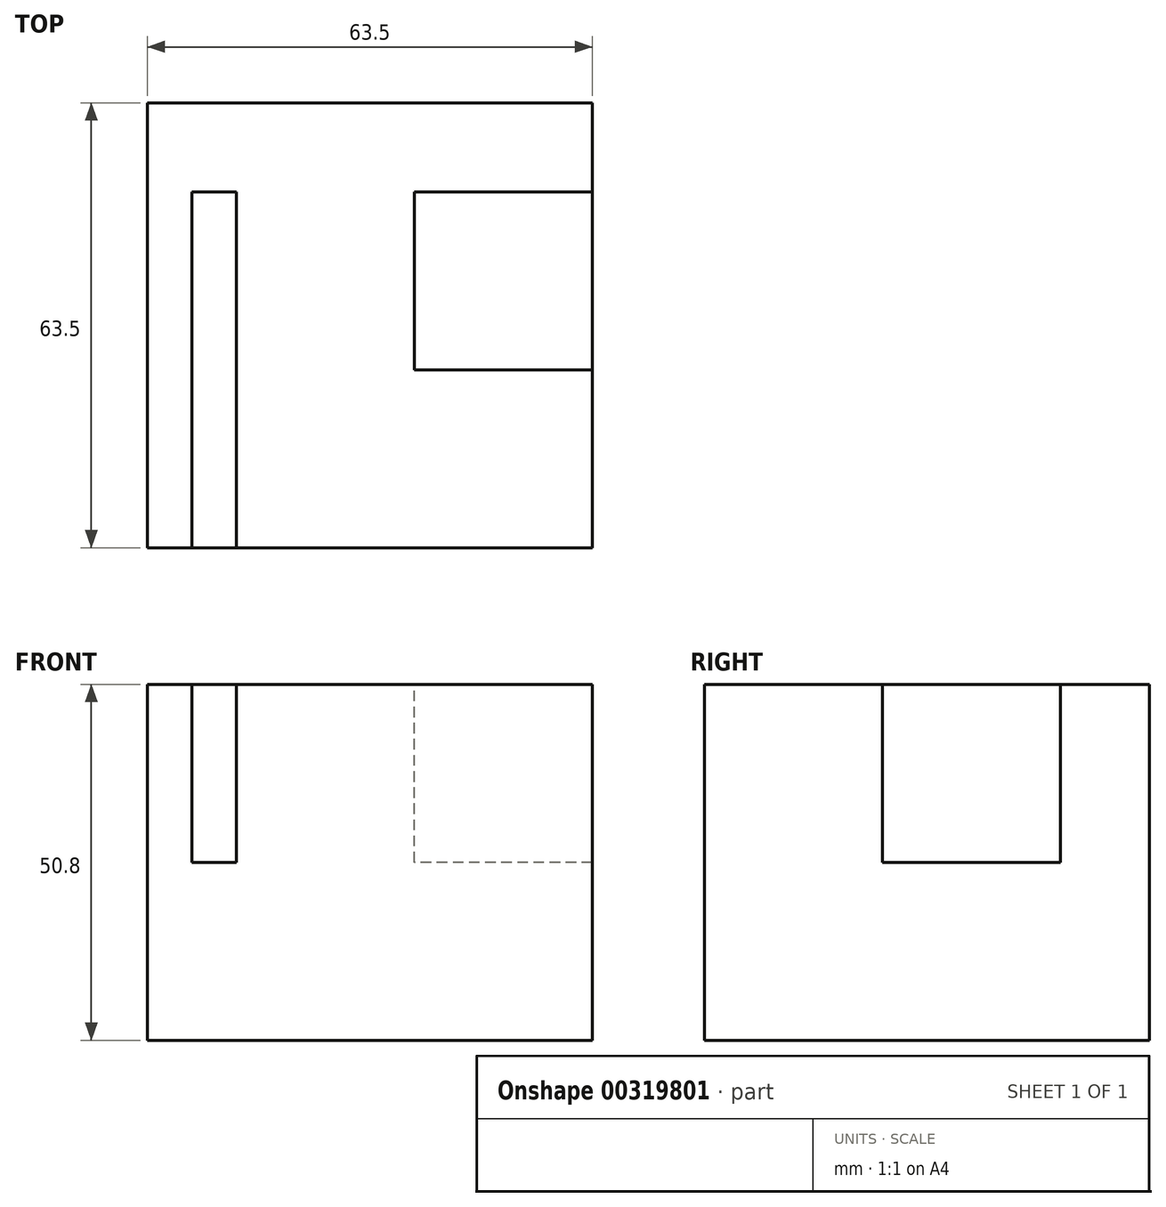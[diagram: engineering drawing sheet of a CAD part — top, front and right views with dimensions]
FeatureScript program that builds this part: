
annotation { "Feature Type Name" : "Feature", "Feature Type Description" : "" }
export const myFeature = defineFeature(function(context is Context, id is Id, definition is map)
    precondition{}
    {
        {
            var Q0;
            Q0=qCreatedBy(makeId("Top.planeOp"),FACE);
            var sketch = newSketch(context, id + "F0", { "sketchPlane" : qUnion([Q0])});
            skLineSegment(sketch, "E0", {"start": v(-27.31, 38.38) * mm, "end": v(36.19, 38.38) * mm});
            skLineSegment(sketch, "E1", {"start": v(36.19, 38.38) * mm, "end": v(36.19, -25.12) * mm});
            skLineSegment(sketch, "E2", {"start": v(36.19, -25.12) * mm, "end": v(-27.31, -25.12) * mm});
            skLineSegment(sketch, "E3", {"start": v(-27.31, -25.12) * mm, "end": v(-27.31, 38.38) * mm});
            skSolve(sketch);
        }
        {
            var Q0;
            Q0=makeQuery(id+"F0.imprint","IMPRINT",FACE,{"disambiguationData":[TD([[makeQuery(id+"F0.imprint","IMPRINT",EDGE,{"derivedFrom":sQuery(id+"F0.wireOp",EDGE,"E0")}),-1.0]])]});
            extrude(context, id + "F1", {"entities" : qUnion([Q0]), "depth" : 50.8 * mm});
        }
        {
            var Q0;
            Q0=makeQuery(id+"F1.opExtrude","CAP_FACE",FACE,{"disambiguationData":[OSD([sQuery(id+"F0.wireOp",EDGE,"E0"),sQuery(id+"F0.wireOp",EDGE,"E1"),sQuery(id+"F0.wireOp",EDGE,"E2"),sQuery(id+"F0.wireOp",EDGE,"E3")])],"isStart":false});
            var sketch = newSketch(context, id + "F2", { "sketchPlane" : qUnion([Q0])});
            skLineSegment(sketch, "E4", {"start": v(-20.96, -25.12) * mm, "end": v(-20.96, 25.68) * mm});
            skLineSegment(sketch, "E5", {"start": v(-20.96, 25.68) * mm, "end": v(-14.61, 25.68) * mm});
            skLineSegment(sketch, "E6", {"start": v(-14.61, 25.68) * mm, "end": v(-14.61, -25.12) * mm});
            skSolve(sketch);
        }
        {
            var Q0;
            {var subQ0=sQuery(id+"F2.wireOp",EDGE,"E4");Q0=makeQuery(id+"F2.imprint","IMPRINT",FACE,{"disambiguationData":[TD([[makeQuery(id+"F2.imprint","IMPRINT",EDGE,{"derivedFrom":subQ0}),-1.0]])]});}
            extrude(context, id + "F3", {"entities" : qUnion([Q0]), "operationType" : NewBodyOperationType.REMOVE, "oppositeDirection" : true, "depth" : 25.4 * mm});
        }
        {
            var Q0;
            Q0=makeQuery(id+"F1.opExtrude","CAP_FACE",FACE,{"disambiguationData":[OSD([sQuery(id+"F0.wireOp",EDGE,"E0"),sQuery(id+"F0.wireOp",EDGE,"E1"),sQuery(id+"F0.wireOp",EDGE,"E2"),sQuery(id+"F0.wireOp",EDGE,"E3")])],"isStart":false});
            var sketch = newSketch(context, id + "F4", { "sketchPlane" : qUnion([Q0])});
            skLineSegment(sketch, "E7", {"start": v(36.19, 0.28) * mm, "end": v(10.79, 0.28) * mm});
            skLineSegment(sketch, "E8", {"start": v(10.79, 0.28) * mm, "end": v(10.79, 25.68) * mm});
            skLineSegment(sketch, "E9", {"start": v(10.79, 25.68) * mm, "end": v(36.19, 25.68) * mm});
            skSolve(sketch);
        }
        {
            var Q0;
            {var subQ0=sQuery(id+"F4.wireOp",EDGE,"E7");Q0=makeQuery(id+"F4.imprint","IMPRINT",FACE,{"disambiguationData":[TD([[makeQuery(id+"F4.imprint","IMPRINT",EDGE,{"derivedFrom":subQ0}),-1.0]])]});}
            extrude(context, id + "F5", {"entities" : qUnion([Q0]), "operationType" : NewBodyOperationType.REMOVE, "oppositeDirection" : true, "depth" : 25.4 * mm});
        }
    });
